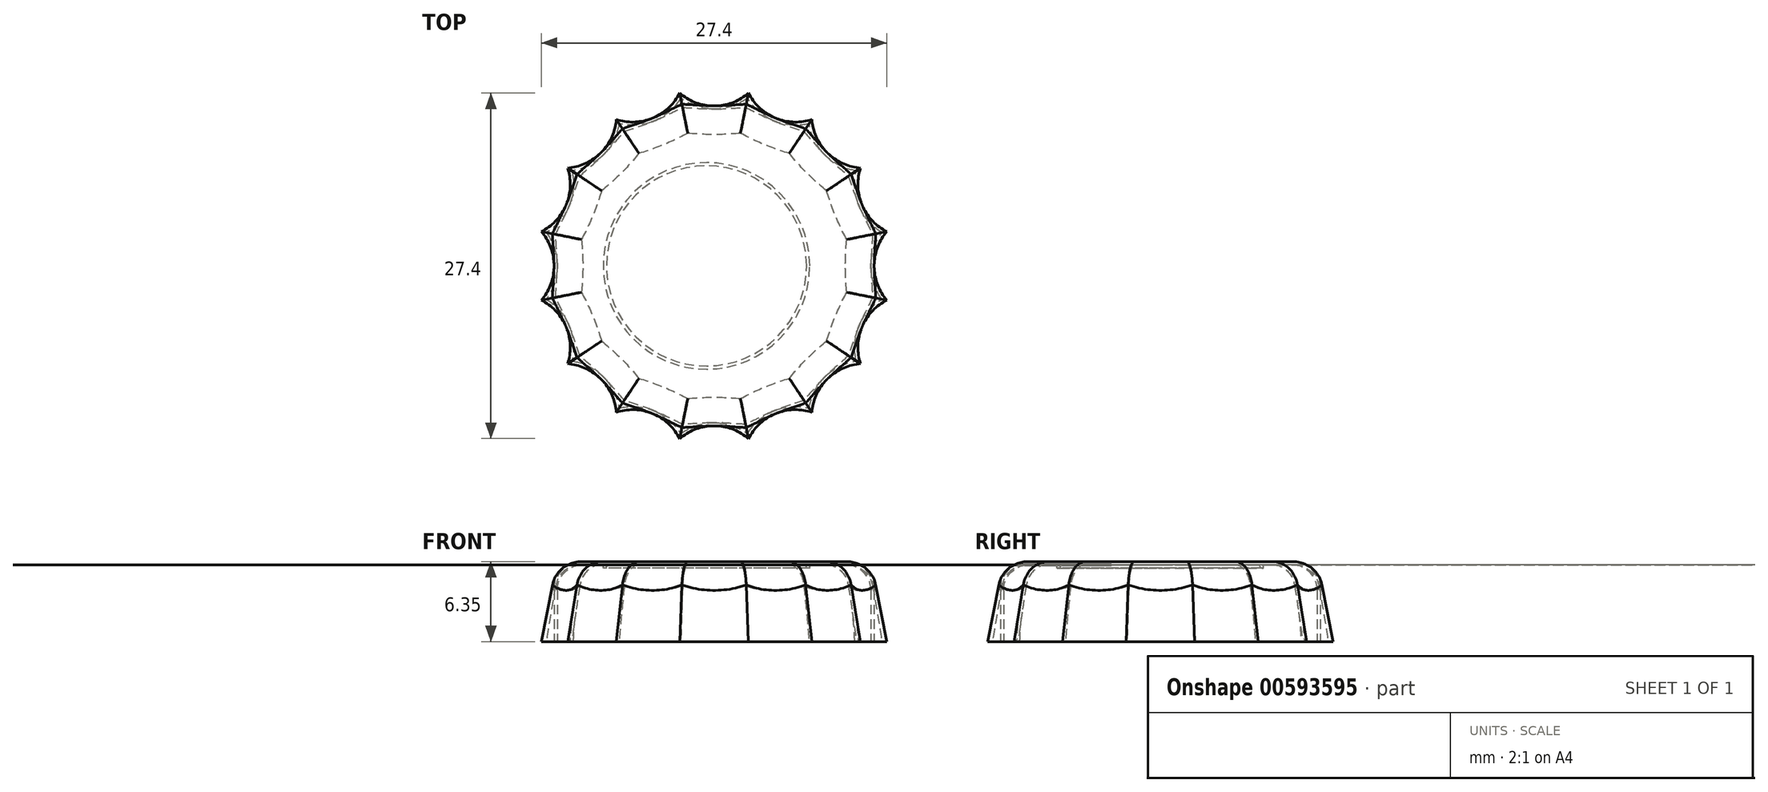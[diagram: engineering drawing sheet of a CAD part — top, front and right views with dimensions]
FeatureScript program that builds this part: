
annotation { "Feature Type Name" : "Feature", "Feature Type Description" : "" }
export const myFeature = defineFeature(function(context is Context, id is Id, definition is map)
    precondition{}
    {
        {
            var Q0;
            Q0=qCreatedBy(makeId("Top.planeOp"),FACE);
            var sketch = newSketch(context, id + "F0", { "sketchPlane" : qUnion([Q0])});
            skCircle(sketch, "E0", {"center": v(0, 0) * mm, "radius": 12.7 * mm, "construction": true});
            skCircle(sketch, "E1.0", {"center": v(0, 0) * mm, "radius": 13.97 * mm});
            skArc(sketch, "E2", {"start": v(-2.73, 13.7) * mm, "mid": v(0, 12.7) * mm, "end": v(2.73, 13.7) * mm});
            skArc(sketch, "E3.1.0", {"start": v(-7.76, 11.62) * mm, "mid": v(-4.86, 11.73) * mm, "end": v(-2.73, 13.7) * mm});
            skArc(sketch, "E3.2.0", {"start": v(-11.62, 7.76) * mm, "mid": v(-8.98, 8.98) * mm, "end": v(-7.76, 11.62) * mm});
            skArc(sketch, "E3.3.0", {"start": v(-13.7, 2.73) * mm, "mid": v(-11.73, 4.86) * mm, "end": v(-11.62, 7.76) * mm});
            skArc(sketch, "E3.4.0", {"start": v(-13.7, -2.73) * mm, "mid": v(-12.7, 0) * mm, "end": v(-13.7, 2.73) * mm});
            skArc(sketch, "E3.5.0", {"start": v(-11.62, -7.76) * mm, "mid": v(-11.73, -4.86) * mm, "end": v(-13.7, -2.73) * mm});
            skArc(sketch, "E3.6.0", {"start": v(-7.76, -11.62) * mm, "mid": v(-8.98, -8.98) * mm, "end": v(-11.62, -7.76) * mm});
            skArc(sketch, "E3.7.0", {"start": v(-2.73, -13.7) * mm, "mid": v(-4.86, -11.73) * mm, "end": v(-7.76, -11.62) * mm});
            skArc(sketch, "E3.8.0", {"start": v(2.73, -13.7) * mm, "mid": v(0, -12.7) * mm, "end": v(-2.73, -13.7) * mm});
            skArc(sketch, "E3.9.0", {"start": v(7.76, -11.62) * mm, "mid": v(4.86, -11.73) * mm, "end": v(2.73, -13.7) * mm});
            skArc(sketch, "E3.10.0", {"start": v(11.62, -7.76) * mm, "mid": v(8.98, -8.98) * mm, "end": v(7.76, -11.62) * mm});
            skArc(sketch, "E3.11.0", {"start": v(13.7, -2.73) * mm, "mid": v(11.73, -4.86) * mm, "end": v(11.62, -7.76) * mm});
            skArc(sketch, "E3.12.0", {"start": v(13.7, 2.73) * mm, "mid": v(12.7, 0) * mm, "end": v(13.7, -2.73) * mm});
            skArc(sketch, "E3.13.0", {"start": v(11.62, 7.76) * mm, "mid": v(11.73, 4.86) * mm, "end": v(13.7, 2.73) * mm});
            skArc(sketch, "E3.14.0", {"start": v(7.76, 11.62) * mm, "mid": v(8.98, 8.98) * mm, "end": v(11.62, 7.76) * mm});
            skArc(sketch, "E3.15.0", {"start": v(2.73, 13.7) * mm, "mid": v(4.86, 11.73) * mm, "end": v(7.76, 11.62) * mm});
            skSolve(sketch);
        }
        {
            var Q0;
            Q0=makeQuery(id+"F0.imprint","IMPRINT",FACE,{"disambiguationData":[TD([[makeQuery(id+"F0.imprint","IMPRINT",EDGE,{"derivedFrom":sQuery(id+"F0.wireOp",EDGE,"E2")}),-1.0]])]});
            var Q1;
            Q1=qBodyType(qCreatedBy(id+"F2",EDGE),BodyType.WIRE);
            cPlane(context, id + "F1", {"entities" : qUnion([Q0, Q1]), "cplaneType" : CPlaneType.OFFSET, "offset" : 6.35 * mm, "width" : 152.4 * mm, "height" : 152.4 * mm});
        }
        {
            var Q0;
            Q0=qCreatedBy(id+"F1.planeOp",FACE);
            var sketch = newSketch(context, id + "F2", { "sketchPlane" : qUnion([Q0])});
            skCircle(sketch, "E4.0", {"center": v(0, 0) * mm, "radius": 12.7 * mm});
            skSolve(sketch);
        }
        {
            var Q0;
            Q0=makeQuery(id+"F0.imprint","IMPRINT",FACE,{"disambiguationData":[TD([[makeQuery(id+"F0.imprint","IMPRINT",EDGE,{"derivedFrom":sQuery(id+"F0.wireOp",EDGE,"E2")}),-1.0]])]});
            var Q1;
            Q1=makeQuery(id+"F2.imprint","IMPRINT",FACE,{"disambiguationData":[TD([[makeQuery(id+"F2.imprint","IMPRINT",EDGE,{"derivedFrom":sQuery(id+"F2.wireOp",EDGE,"E4.0")}),1.0]])]});
            loft(context, id + "F3", {"sheetProfilesArray" : [{ "sheetProfileEntities" : qUnion([Q0]) }, { "sheetProfileEntities" : qUnion([Q1]) }]});
        }
        {
            var Q0;
            Q0=makeQuery(id+"F3.opLoft","CAP_FACE",FACE,{"disambiguationData":[OSD([makeQuery(id+"F2.imprint","IMPRINT",FACE,{"disambiguationData":[TD([[makeQuery(id+"F2.imprint","IMPRINT",EDGE,{"derivedFrom":sQuery(id+"F2.wireOp",EDGE,"E4.0")}),1.0]])]})])],"isStart":true});
            fillet(context, id + "F4", {"entities" : qUnion([Q0]), "radius" : 2.3 * mm, "tangentPropagation" : true, "allowEdgeOverflow" : false});
        }
        {
            var Q0;
            Q0=makeQuery(id+"F3.opLoft","CAP_FACE",FACE,{"disambiguationData":[OSD([makeQuery(id+"F0.imprint","IMPRINT",FACE,{"disambiguationData":[TD([[makeQuery(id+"F0.imprint","IMPRINT",EDGE,{"derivedFrom":sQuery(id+"F0.wireOp",EDGE,"E2")}),-1.0]])]})])],"isStart":true});
            shell(context, id + "F5", {"entities" : qUnion([Q0]), "thickness" : 0.25 * mm});
        }
        {
            var Q0;
            Q0=makeQuery(id+"F3.opLoft","CAP_FACE",FACE,{"disambiguationData":[OSD([makeQuery(id+"F2.imprint","IMPRINT",FACE,{"disambiguationData":[TD([[makeQuery(id+"F2.imprint","IMPRINT",EDGE,{"derivedFrom":sQuery(id+"F2.wireOp",EDGE,"E4.0")}),1.0]])]})])],"isStart":true});
            cPlane(context, id + "F6", {"entities" : qUnion([Q0]), "cplaneType" : CPlaneType.OFFSET, "offset" : 0.25 * mm, "oppositeDirection" : true, "width" : 152.4 * mm, "height" : 152.4 * mm});
        }
        {
            var Q0;
            Q0=qCreatedBy(id+"F6.planeOp",FACE);
            var sketch = newSketch(context, id + "F7", { "sketchPlane" : qUnion([Q0])});
            skCircle(sketch, "E5", {"center": v(-0.6, 0) * mm, "radius": 7.94 * mm});
            skCircle(sketch, "E6.0", {"center": v(-0.6, 0) * mm, "radius": 8.2 * mm});
            skSolve(sketch);
        }
        {
            var Q0;
            Q0=qSketchRegion(id+"F7",true);
            extrude(context, id + "F8", {"entities" : qUnion([Q0]), "operationType" : NewBodyOperationType.ADD, "oppositeDirection" : true, "depth" : 0.25 * mm});
        }
        {
            var Q0;
            Q0=makeQuery(id+"F8.opExtrude","CAP_EDGE",EDGE,{"disambiguationData":[OSD([sQuery(id+"F7.wireOp",EDGE,"E6.0")])],"isStart":true});
            var Q1;
            Q1=makeQuery(id+"F8.opExtrude","CAP_EDGE",EDGE,{"disambiguationData":[OSD([sQuery(id+"F7.wireOp",EDGE,"E5")])],"isStart":true});
            fillet(context, id + "F9", {"entities" : qUnion([Q0, Q1]), "radius" : 0.25 * mm, "tangentPropagation" : true, "allowEdgeOverflow" : false});
        }
    });
